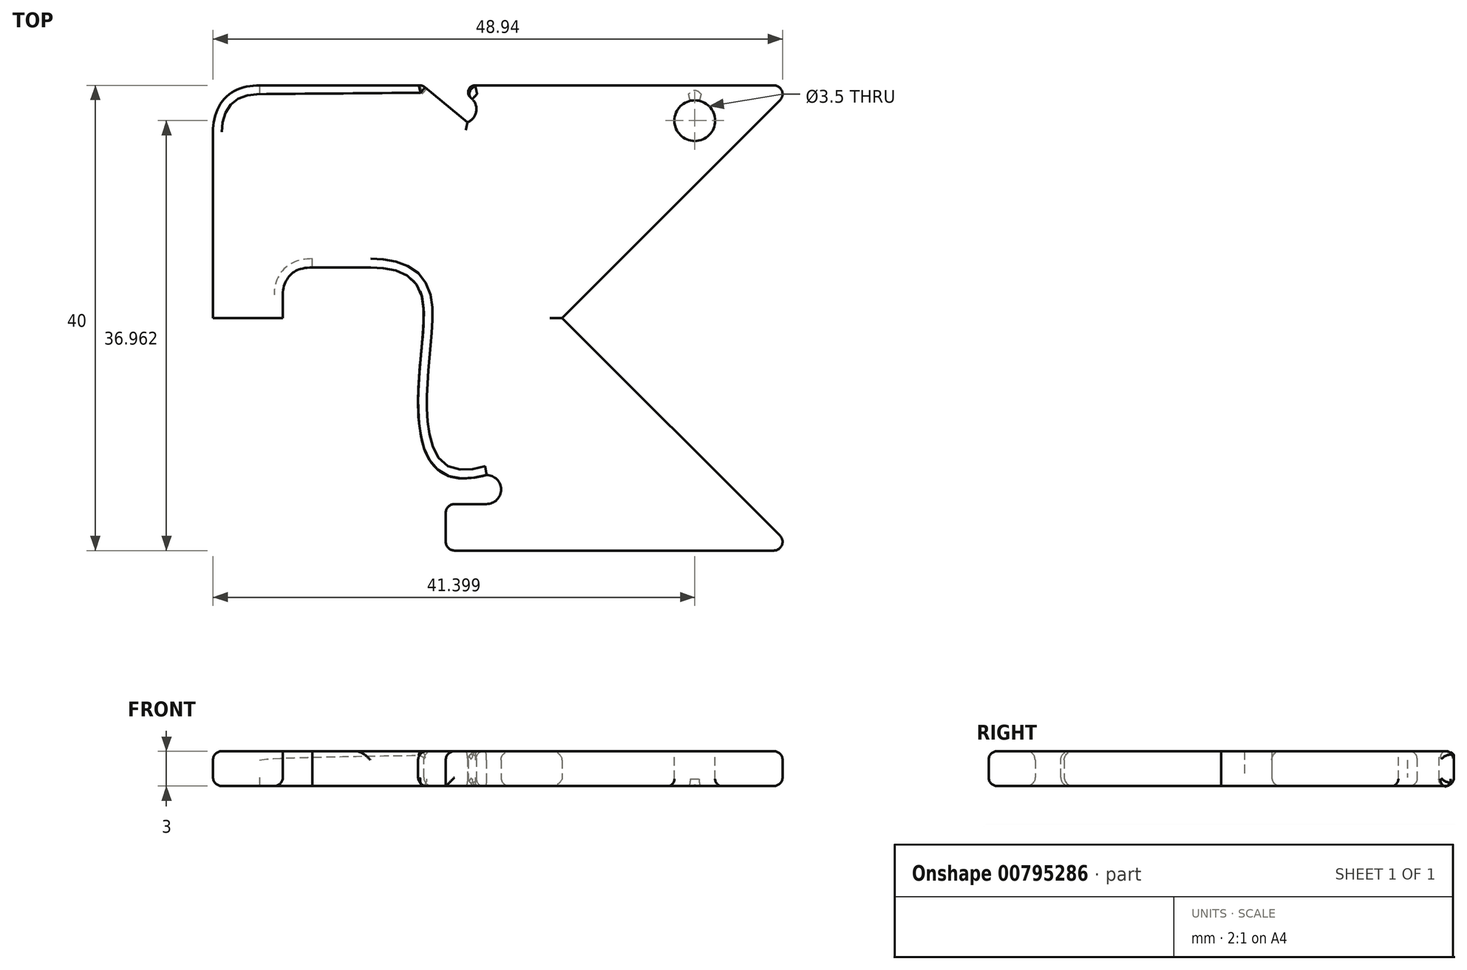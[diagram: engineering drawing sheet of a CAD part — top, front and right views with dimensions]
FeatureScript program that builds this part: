
annotation { "Feature Type Name" : "Feature", "Feature Type Description" : "" }
export const myFeature = defineFeature(function(context is Context, id is Id, definition is map)
    precondition{}
    {
        {
            var Q0;
            Q0=qCreatedBy(makeId("Top.planeOp"),FACE);
            var sketch = newSketch(context, id + "F0", { "sketchPlane" : qUnion([Q0])});
            skLineSegment(sketch, "E0", {"start": v(0, 0) * mm, "end": v(-25, 0) * mm, "construction": true});
            skLineSegment(sketch, "E1", {"start": v(0, 0) * mm, "end": v(25, 0) * mm, "construction": true});
            skLineSegment(sketch, "E2", {"start": v(0, 0) * mm, "end": v(0, 30) * mm, "construction": true});
            skLineSegment(sketch, "E3", {"start": v(0, 0) * mm, "end": v(0, -30) * mm, "construction": true});
            skLineSegment(sketch, "E4", {"start": v(25, 0) * mm, "end": v(25, 20) * mm, "construction": true});
            skLineSegment(sketch, "E5", {"start": v(25, 0) * mm, "end": v(25, -20) * mm, "construction": true});
            skLineSegment(sketch, "E6", {"start": v(-25, 0) * mm, "end": v(-25, 20) * mm, "construction": true});
            skLineSegment(sketch, "E7", {"start": v(-25, 20) * mm, "end": v(-25, 16) * mm, "construction": true});
            skLineSegment(sketch, "E8", {"start": v(-25, 20) * mm, "end": v(-21, 20) * mm, "construction": true});
            skLineSegment(sketch, "E9", {"start": v(-25, 20) * mm, "end": v(-7, 20) * mm, "construction": true});
            skLineSegment(sketch, "E10", {"start": v(25, -20) * mm, "end": v(-5, -20) * mm, "construction": true});
            skLineSegment(sketch, "E11", {"start": v(-5, -20) * mm, "end": v(-5, -16) * mm, "construction": true});
            skLineSegment(sketch, "E12", {"start": v(-25, 0) * mm, "end": v(-19, 0) * mm});
            skLineSegment(sketch, "E13", {"start": v(-19, 0) * mm, "end": v(-19, 2) * mm});
            skFitSpline(sketch, "E14", {"points": [v(-19, 2) * mm, v(-18.33, 3.72) * mm, v(-16.47, 4.34) * mm], "startDerivative": vector(-0.06, 4.76) * mm, "endDerivative": vector(5.58, 0.07) * mm});
            skFitSpline(sketch, "E15", {"points": [v(-25, 16) * mm, v(-23.92, 18.98) * mm, v(-21, 20) * mm], "startDerivative": vector(-0.06, 6.39) * mm, "endDerivative": vector(6.8, 0.05) * mm});
            skLineSegment(sketch, "E16", {"start": v(-25, 0) * mm, "end": v(-25, 16) * mm});
            skLineSegment(sketch, "E17", {"start": v(-21, 20) * mm, "end": v(-7, 20) * mm});
            skLineSegment(sketch, "E18", {"start": v(-7, 20) * mm, "end": v(-3.14, 16.82) * mm});
            skLineSegment(sketch, "E19", {"start": v(25, 20) * mm, "end": v(-4.2, 20) * mm});
            skLineSegment(sketch, "E20", {"start": v(-4.2, 20) * mm, "end": v(-2.83, 18.91) * mm});
            skArc(sketch, "E21", {"start": v(-3.14, 16.82) * mm, "mid": v(-2.38, 17.78) * mm, "end": v(-2.83, 18.91) * mm});
            skLineSegment(sketch, "E22", {"start": v(25, 20) * mm, "end": v(5, 0) * mm, "construction": true});
            skLineSegment(sketch, "E23", {"start": v(5, 0) * mm, "end": v(25, -20) * mm, "construction": true});
            skLineSegment(sketch, "E24", {"start": v(25, 20) * mm, "end": v(5, 0) * mm});
            skLineSegment(sketch, "E25", {"start": v(5, 0) * mm, "end": v(25, -20) * mm});
            skLineSegment(sketch, "E26", {"start": v(25, -20) * mm, "end": v(-5, -20) * mm});
            skLineSegment(sketch, "E27", {"start": v(-5, -16) * mm, "end": v(-1.5, -16) * mm});
            skLineSegment(sketch, "E28", {"start": v(-1.5, -16) * mm, "end": v(-1.5, -13.5) * mm, "construction": true});
            skLineSegment(sketch, "E29", {"start": v(-16.47, 4.34) * mm, "end": v(-11.47, 4.34) * mm});
            skFitSpline(sketch, "E30", {"points": [v(-1.5, -13.5) * mm, v(-7.12, -2.97) * mm, v(-11.47, 4.34) * mm], "startDerivative": vector(-36.55, -10.35) * mm, "endDerivative": vector(-33.91, 0.5) * mm});
            skArc(sketch, "E31", {"start": v(-1.5, -16) * mm, "mid": v(-0.25, -14.75) * mm, "end": v(-1.5, -13.5) * mm});
            skLineSegment(sketch, "E32", {"start": v(-5, -16) * mm, "end": v(-5, -20) * mm});
            skSolve(sketch);
        }
        {
            var Q0;
            Q0=makeQuery(id+"F0.imprint","IMPRINT",FACE,{"disambiguationData":[TD([[makeQuery(id+"F0.imprint","IMPRINT",EDGE,{"derivedFrom":sQuery(id+"F0.wireOp",EDGE,"E12")}),1.0]])]});
            extrude(context, id + "F1", {"entities" : qUnion([Q0]), "flatOperationType" : FlatOperationType.REMOVE, "depth" : 3 * mm, "offsetDistance" : 25 * mm, "domain" : OperationDomain.MODEL});
        }
        {
            var Q0;
            Q0=makeQuery(id+"F1.opExtrude","SWEPT_EDGE",EDGE,{"disambiguationData":[OSD([sQuery(id+"F0.wireOp",EDGE,"E25"),sQuery(id+"F0.wireOp",EDGE,"E26")])]});
            var Q1;
            Q1=makeQuery(id+"F1.opExtrude","SWEPT_EDGE",EDGE,{"disambiguationData":[OSD([sQuery(id+"F0.wireOp",EDGE,"E19"),sQuery(id+"F0.wireOp",EDGE,"E24")])]});
            var Q2;
            Q2=makeQuery(id+"F1.opExtrude","SWEPT_EDGE",EDGE,{"disambiguationData":[OSD([sQuery(id+"F0.wireOp",EDGE,"E27"),sQuery(id+"F0.wireOp",EDGE,"E32")])]});
            var Q3;
            Q3=makeQuery(id+"F1.opExtrude","SWEPT_EDGE",EDGE,{"disambiguationData":[OSD([sQuery(id+"F0.wireOp",EDGE,"E29"),sQuery(id+"F0.wireOp",EDGE,"E30")])]});
            var Q4;
            Q4=makeQuery(id+"F1.opExtrude","CAP_EDGE",EDGE,{"disambiguationData":[OSD([sQuery(id+"F0.wireOp",EDGE,"E16")])],"isStart":false});
            var Q5;
            Q5=makeQuery(id+"F1.opExtrude","CAP_EDGE",EDGE,{"disambiguationData":[OSD([sQuery(id+"F0.wireOp",EDGE,"E15")])],"isStart":false});
            var Q6;
            Q6=makeQuery(id+"F1.opExtrude","CAP_EDGE",EDGE,{"disambiguationData":[OSD([sQuery(id+"F0.wireOp",EDGE,"E19")])],"isStart":false});
            var Q7;
            Q7=makeQuery(id+"F1.opExtrude","CAP_EDGE",EDGE,{"disambiguationData":[OSD([sQuery(id+"F0.wireOp",EDGE,"E24")])],"isStart":false});
            var Q8;
            Q8=makeQuery(id+"F1.opExtrude","CAP_EDGE",EDGE,{"disambiguationData":[OSD([sQuery(id+"F0.wireOp",EDGE,"E25")])],"isStart":false});
            var Q9;
            Q9=makeQuery(id+"F1.opExtrude","CAP_EDGE",EDGE,{"disambiguationData":[OSD([sQuery(id+"F0.wireOp",EDGE,"E26")])],"isStart":false});
            var Q10;
            Q10=makeQuery(id+"F1.opExtrude","CAP_EDGE",EDGE,{"disambiguationData":[OSD([sQuery(id+"F0.wireOp",EDGE,"E32")])],"isStart":false});
            var Q11;
            Q11=makeQuery(id+"F1.opExtrude","CAP_EDGE",EDGE,{"disambiguationData":[OSD([sQuery(id+"F0.wireOp",EDGE,"E27")])],"isStart":false});
            var Q12;
            Q12=makeQuery(id+"F1.opExtrude","CAP_EDGE",EDGE,{"disambiguationData":[OSD([sQuery(id+"F0.wireOp",EDGE,"E30")])],"isStart":false});
            var Q13;
            Q13=makeQuery(id+"F1.opExtrude","CAP_EDGE",EDGE,{"disambiguationData":[OSD([sQuery(id+"F0.wireOp",EDGE,"E31")])],"isStart":false});
            var Q14;
            Q14=makeQuery(id+"F1.opExtrude","CAP_EDGE",EDGE,{"disambiguationData":[OSD([sQuery(id+"F0.wireOp",EDGE,"E19")])],"isStart":true});
            var Q15;
            Q15=makeQuery(id+"F1.opExtrude","CAP_EDGE",EDGE,{"disambiguationData":[OSD([sQuery(id+"F0.wireOp",EDGE,"E17")])],"isStart":true});
            var Q16;
            Q16=makeQuery(id+"F1.opExtrude","CAP_EDGE",EDGE,{"disambiguationData":[OSD([sQuery(id+"F0.wireOp",EDGE,"E15")])],"isStart":true});
            var Q17;
            Q17=makeQuery(id+"F1.opExtrude","CAP_EDGE",EDGE,{"disambiguationData":[OSD([sQuery(id+"F0.wireOp",EDGE,"E13")])],"isStart":true});
            var Q18;
            Q18=makeQuery(id+"F1.opExtrude","CAP_EDGE",EDGE,{"disambiguationData":[OSD([sQuery(id+"F0.wireOp",EDGE,"E14")])],"isStart":true});
            var Q19;
            Q19=makeQuery(id+"F1.opExtrude","CAP_EDGE",EDGE,{"disambiguationData":[OSD([sQuery(id+"F0.wireOp",EDGE,"E29")])],"isStart":true});
            var Q20;
            Q20=makeQuery(id+"F1.opExtrude","CAP_EDGE",EDGE,{"disambiguationData":[OSD([sQuery(id+"F0.wireOp",EDGE,"E16")])],"isStart":true});
            var Q21;
            Q21=makeQuery(id+"F1.opExtrude","CAP_EDGE",EDGE,{"disambiguationData":[OSD([sQuery(id+"F0.wireOp",EDGE,"E30")])],"isStart":true});
            var Q22;
            Q22=makeQuery(id+"F1.opExtrude","CAP_EDGE",EDGE,{"disambiguationData":[OSD([sQuery(id+"F0.wireOp",EDGE,"E31")])],"isStart":true});
            var Q23;
            Q23=makeQuery(id+"F1.opExtrude","CAP_EDGE",EDGE,{"disambiguationData":[OSD([sQuery(id+"F0.wireOp",EDGE,"E27")])],"isStart":true});
            var Q24;
            Q24=makeQuery(id+"F1.opExtrude","CAP_EDGE",EDGE,{"disambiguationData":[OSD([sQuery(id+"F0.wireOp",EDGE,"E24")])],"isStart":true});
            var Q25;
            Q25=makeQuery(id+"F1.opExtrude","CAP_EDGE",EDGE,{"disambiguationData":[OSD([sQuery(id+"F0.wireOp",EDGE,"E25")])],"isStart":true});
            var Q26;
            Q26=makeQuery(id+"F1.opExtrude","CAP_EDGE",EDGE,{"disambiguationData":[OSD([sQuery(id+"F0.wireOp",EDGE,"E26")])],"isStart":true});
            var Q27;
            Q27=makeQuery(id+"F1.opExtrude","SWEPT_EDGE",EDGE,{"disambiguationData":[OSD([sQuery(id+"F0.wireOp",EDGE,"E26"),sQuery(id+"F0.wireOp",EDGE,"E32")])]});
            fillet(context, id + "F2", {"entities" : qUnion([Q0, Q1, Q2, Q3, Q4, Q5, Q6, Q7, Q8, Q9, Q10, Q11, Q12, Q13, Q14, Q15, Q16, Q17, Q18, Q19, Q20, Q21, Q22, Q23, Q24, Q25, Q26, Q27]), "radius" : .75 * mm, "tangentPropagation" : true, "allowEdgeOverflow" : false});
        }
        {
            var Q0;
            Q0=makeQuery(id+"F1.opExtrude","CAP_FACE",FACE,{"disambiguationData":[OSD([sQuery(id+"F0.wireOp",EDGE,"E12"),sQuery(id+"F0.wireOp",EDGE,"E13"),sQuery(id+"F0.wireOp",EDGE,"E14"),sQuery(id+"F0.wireOp",EDGE,"E15"),sQuery(id+"F0.wireOp",EDGE,"E16"),sQuery(id+"F0.wireOp",EDGE,"E17"),sQuery(id+"F0.wireOp",EDGE,"E18"),sQuery(id+"F0.wireOp",EDGE,"E19"),sQuery(id+"F0.wireOp",EDGE,"E20"),sQuery(id+"F0.wireOp",EDGE,"E21"),sQuery(id+"F0.wireOp",EDGE,"E24"),sQuery(id+"F0.wireOp",EDGE,"E25"),sQuery(id+"F0.wireOp",EDGE,"E26"),sQuery(id+"F0.wireOp",EDGE,"E27"),sQuery(id+"F0.wireOp",EDGE,"E29"),sQuery(id+"F0.wireOp",EDGE,"E30"),sQuery(id+"F0.wireOp",EDGE,"E31"),sQuery(id+"F0.wireOp",EDGE,"E32")])],"isStart":false});
            var sketch = newSketch(context, id + "F3", { "sketchPlane" : qUnion([Q0])});
            skCircle(sketch, "E33", {"center": v(16.4, 16.96) * mm, "radius": 1.75 * mm});
            skSolve(sketch);
        }
        {
            var Q0;
            Q0 = qSketchRegion(id + "F3", true);
            extrude(context, id + "F4", {"entities" : qUnion([Q0]), "operationType" : NewBodyOperationType.REMOVE, "endBound" : BoundingType.THROUGH_ALL, "oppositeDirection" : true, "depth" : 25 * mm, "offsetDistance" : 25 * mm});
        }
        {
            var Q0;
            Q0=makeQuery(id+"F4.boolean.opBoolean","COPY",EDGE,{"derivedFrom":makeQuery(id+"F4.opExtrude","CAP_EDGE",EDGE,{"disambiguationData":[OSD([sQuery(id+"F3.wireOp",EDGE,"E33")])],"isStart":true})});
            var Q1;
            Q1=makeQuery(id+"F4.boolean.opBoolean","INTERSECT",EDGE,{"derivedFrom":[makeQuery(id+"F1.opExtrude","CAP_FACE",FACE,{"disambiguationData":[OSD([sQuery(id+"F0.wireOp",EDGE,"E12"),sQuery(id+"F0.wireOp",EDGE,"E13"),sQuery(id+"F0.wireOp",EDGE,"E14"),sQuery(id+"F0.wireOp",EDGE,"E15"),sQuery(id+"F0.wireOp",EDGE,"E16"),sQuery(id+"F0.wireOp",EDGE,"E17"),sQuery(id+"F0.wireOp",EDGE,"E18"),sQuery(id+"F0.wireOp",EDGE,"E19"),sQuery(id+"F0.wireOp",EDGE,"E20"),sQuery(id+"F0.wireOp",EDGE,"E21"),sQuery(id+"F0.wireOp",EDGE,"E24"),sQuery(id+"F0.wireOp",EDGE,"E25"),sQuery(id+"F0.wireOp",EDGE,"E26"),sQuery(id+"F0.wireOp",EDGE,"E27"),sQuery(id+"F0.wireOp",EDGE,"E29"),sQuery(id+"F0.wireOp",EDGE,"E30"),sQuery(id+"F0.wireOp",EDGE,"E31"),sQuery(id+"F0.wireOp",EDGE,"E32")])],"isStart":true}),makeQuery(id+"F4.opExtrude","SWEPT_FACE",FACE,{"disambiguationData":[OSD([sQuery(id+"F3.wireOp",EDGE,"E33")])]})]});
            var Q2;
            Q2=makeQuery(id+"F1.opExtrude","CAP_EDGE",EDGE,{"disambiguationData":[OSD([sQuery(id+"F0.wireOp",EDGE,"E21")])],"isStart":false});
            var Q3;
            Q3=makeQuery(id+"F1.opExtrude","CAP_EDGE",EDGE,{"disambiguationData":[OSD([sQuery(id+"F0.wireOp",EDGE,"E18")])],"isStart":false});
            var Q4;
            Q4=makeQuery(id+"F1.opExtrude","CAP_EDGE",EDGE,{"disambiguationData":[OSD([sQuery(id+"F0.wireOp",EDGE,"E18")])],"isStart":true});
            var Q5;
            Q5=makeQuery(id+"F1.opExtrude","SWEPT_EDGE",EDGE,{"disambiguationData":[OSD([sQuery(id+"F0.wireOp",EDGE,"E17"),sQuery(id+"F0.wireOp",EDGE,"E18")])]});
            var Q6;
            Q6=makeQuery(id+"F2.opFillet","BLEND_EDGE",EDGE,{"blendedFrom":[makeQuery(id+"F1.opExtrude","CAP_EDGE",EDGE,{"disambiguationData":[OSD([sQuery(id+"F0.wireOp",EDGE,"E15")])],"isStart":false}),makeQuery(id+"F1.opExtrude","SWEPT_FACE",FACE,{"disambiguationData":[OSD([sQuery(id+"F0.wireOp",EDGE,"E18")])]})],"blendedInto":[makeQuery(id+"F1.opExtrude","SWEPT_FACE",FACE,{"disambiguationData":[OSD([sQuery(id+"F0.wireOp",EDGE,"E18")])]})]});
            fillet(context, id + "F5", {"entities" : qUnion([Q0, Q1, Q2, Q3, Q4, Q5, Q6]), "radius" : .6 * mm, "tangentPropagation" : true, "allowEdgeOverflow" : false});
        }
    });
